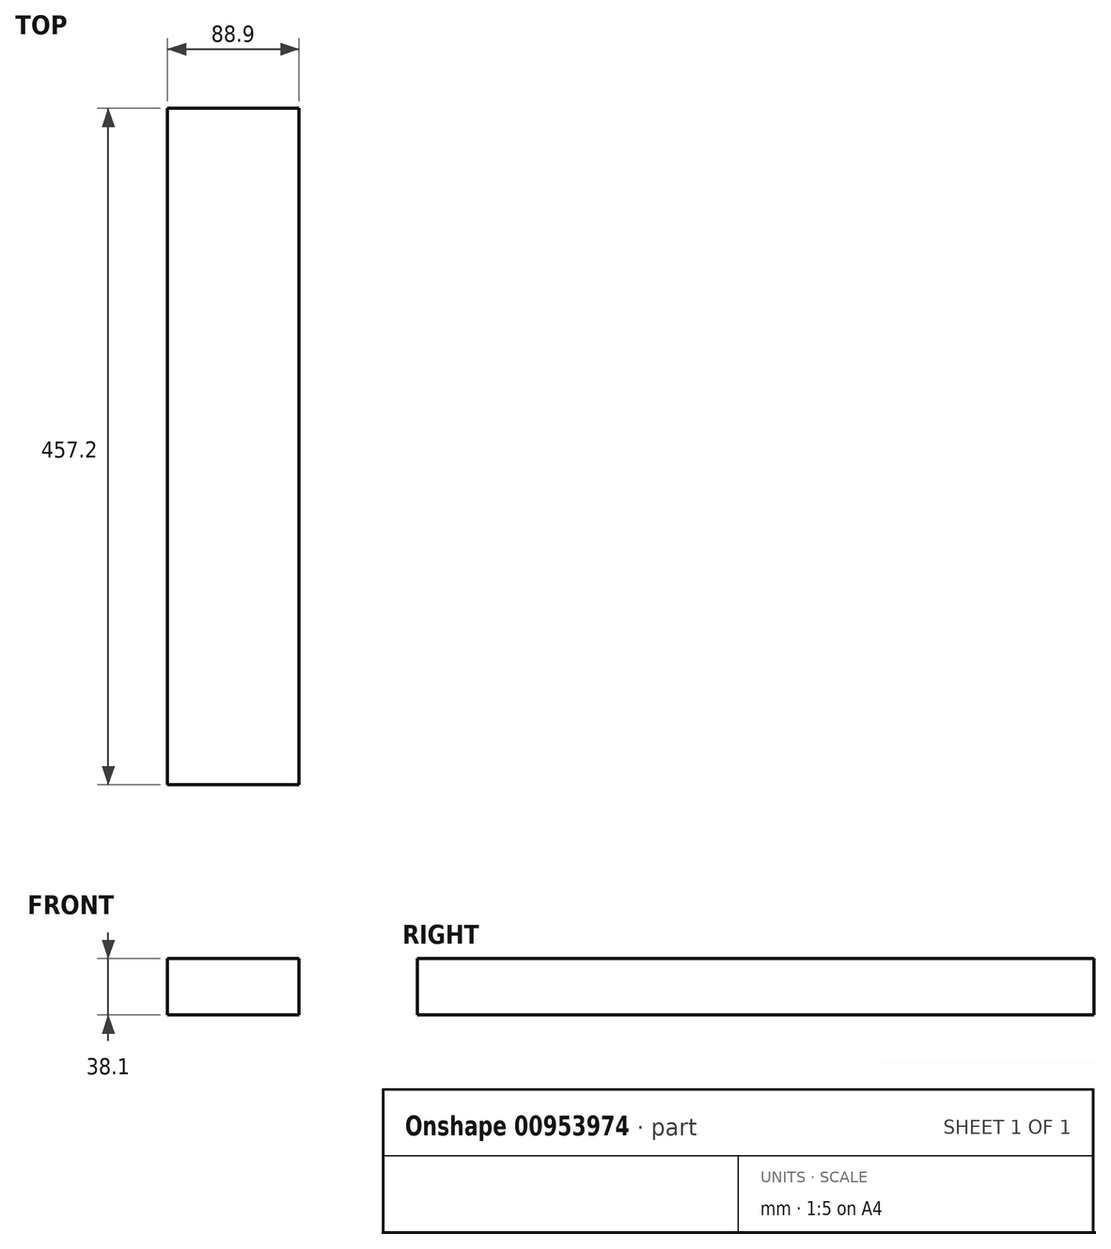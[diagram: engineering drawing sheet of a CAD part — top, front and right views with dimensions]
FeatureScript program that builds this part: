
annotation { "Feature Type Name" : "Feature", "Feature Type Description" : "" }
export const myFeature = defineFeature(function(context is Context, id is Id, definition is map)
    precondition{}
    {
        {
            var Q0;
            Q0=qCreatedBy(makeId("Front.planeOp"),FACE);
            var sketch = newSketch(context, id + "F0", { "sketchPlane" : qUnion([Q0])});
            skLineSegment(sketch, "E0.bottom", {"start": v(44.45, 19.05) * mm, "end": v(-44.45, 19.05) * mm});
            skLineSegment(sketch, "E0.top", {"start": v(44.45, -19.05) * mm, "end": v(-44.45, -19.05) * mm});
            skLineSegment(sketch, "E0.left", {"start": v(44.45, 19.05) * mm, "end": v(44.45, -19.05) * mm});
            skLineSegment(sketch, "E0.right", {"start": v(-44.45, 19.05) * mm, "end": v(-44.45, -19.05) * mm});
            skPoint(sketch, "E0.middle", {"position": v(0, 0) * mm});
            skSolve(sketch);
        }
        {
            var Q0;
            Q0=qSketchRegion(id+"F0",true);
            extrude(context, id + "F1", {"entities" : qUnion([Q0]), "oppositeDirection" : true, "depth" : 457.2 * mm, "offsetDistance" : 25.4 * mm});
        }
    });
